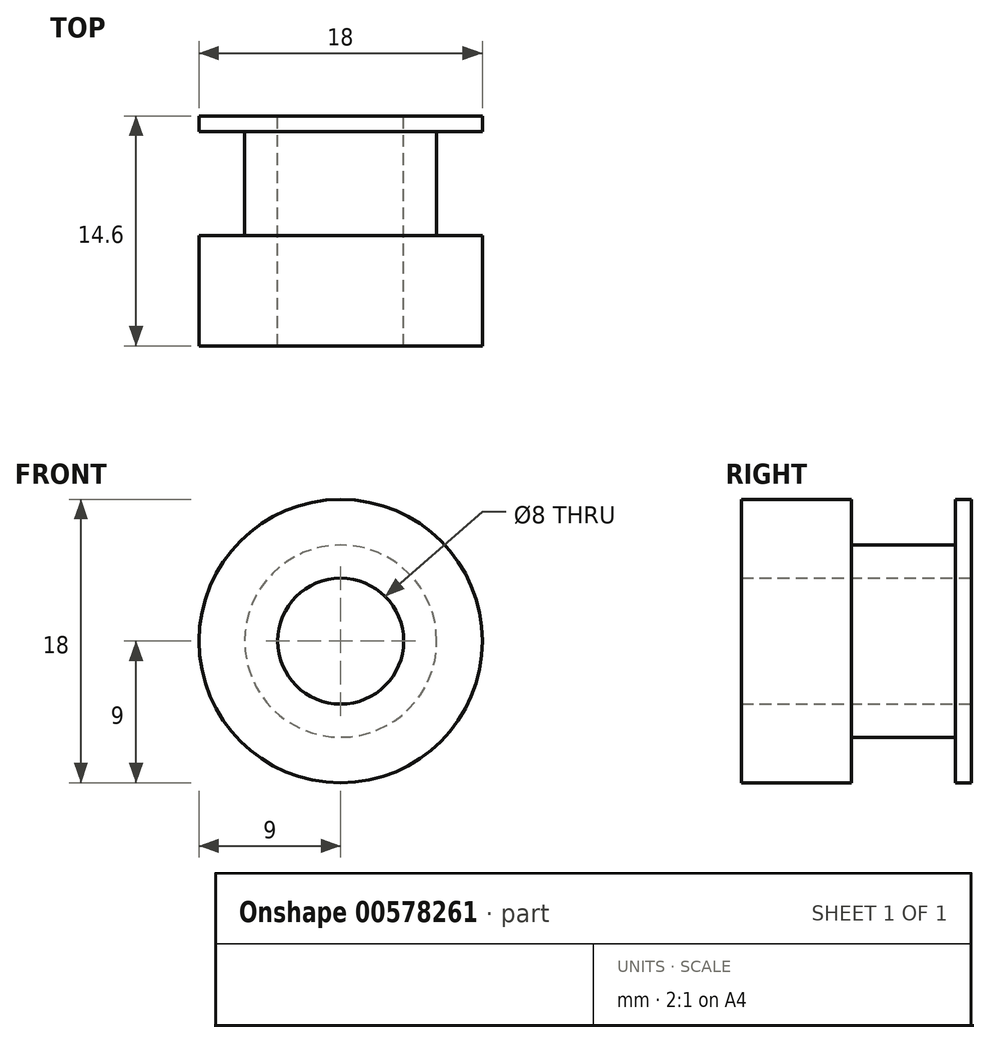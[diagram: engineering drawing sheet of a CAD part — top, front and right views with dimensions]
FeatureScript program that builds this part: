
annotation { "Feature Type Name" : "Feature", "Feature Type Description" : "" }
export const myFeature = defineFeature(function(context is Context, id is Id, definition is map)
    precondition{}
    {
        {
            var Q0;
            Q0=qCreatedBy(makeId("Front.planeOp"),FACE);
            var sketch = newSketch(context, id + "F0", { "sketchPlane" : qUnion([Q0])});
            skCircle(sketch, "E0", {"center": v(0, 0) * mm, "radius": 9 * mm});
            skCircle(sketch, "E1", {"center": v(0, 0) * mm, "radius": 4 * mm});
            skCircle(sketch, "E2", {"center": v(0, 0) * mm, "radius": 6.1 * mm});
            skSolve(sketch);
        }
        {
            var Q0;
            Q0=qSketchRegion(id+"F0",true);
            var Q1;
            Q1=makeQuery(id+"F0.imprint","IMPRINT",FACE,{"disambiguationData":[TD([[makeQuery(id+"F0.imprint","IMPRINT",EDGE,{"derivedFrom":sQuery(id+"F0.wireOp",EDGE,"E1")}),-1.0]])]});
            extrude(context, id + "F1", {"entities" : qUnion([Q0, Q1]), "depth" : 14.6 * mm, "offsetDistance" : 25 * mm});
        }
        {
            var Q0;
            Q0=makeQuery(id+"F0.imprint","IMPRINT",FACE,{"disambiguationData":[TD([[makeQuery(id+"F0.imprint","IMPRINT",EDGE,{"derivedFrom":sQuery(id+"F0.wireOp",EDGE,"E0")}),1.0]])]});
            extrude(context, id + "F2", {"entities" : qUnion([Q0]), "operationType" : NewBodyOperationType.REMOVE, "depth" : 7.6 * mm, "offsetDistance" : 25 * mm, "hasSecondDirection" : true, "secondDirectionOppositeDirection" : false, "secondDirectionDepth" : 1 * mm});
        }
    });
